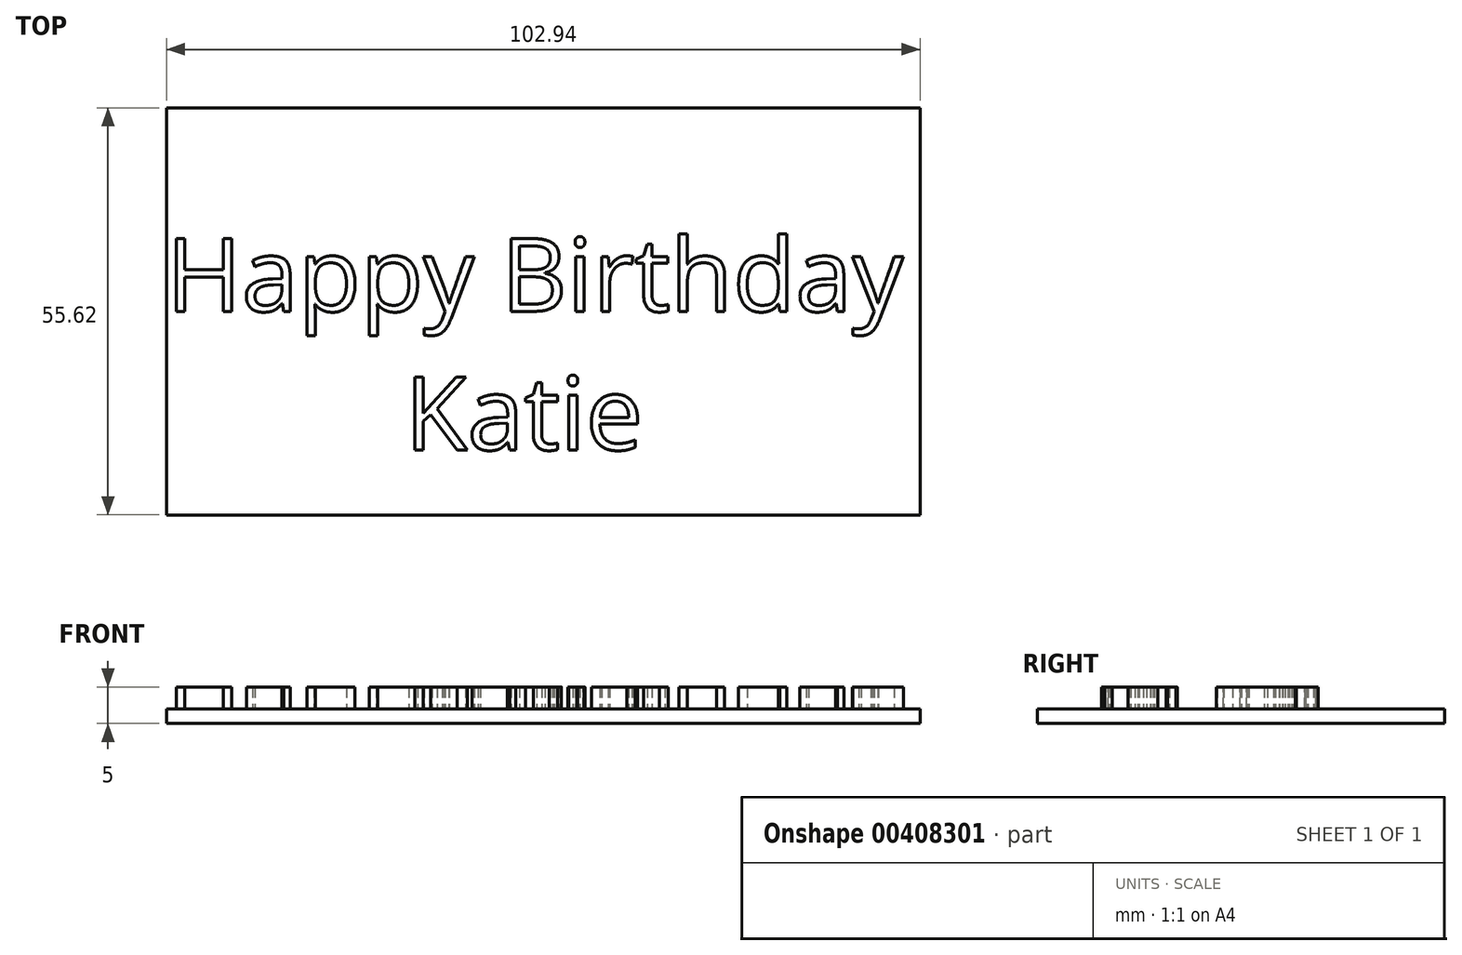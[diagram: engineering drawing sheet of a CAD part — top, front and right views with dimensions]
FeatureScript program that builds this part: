
annotation { "Feature Type Name" : "Feature", "Feature Type Description" : "" }
export const myFeature = defineFeature(function(context is Context, id is Id, definition is map)
    precondition{}
    {
        {
            var Q0;
            Q0=qCreatedBy(makeId("Top.planeOp"),FACE);
            var sketch = newSketch(context, id + "F0", { "sketchPlane" : qUnion([Q0])});
            skLineSegment(sketch, "E0.bottom", {"start": v(-50.3, 25.04) * mm, "end": v(52.64, 25.04) * mm});
            skLineSegment(sketch, "E0.top", {"start": v(-50.3, -30.58) * mm, "end": v(52.64, -30.58) * mm});
            skLineSegment(sketch, "E0.left", {"start": v(-50.3, 25.04) * mm, "end": v(-50.3, -30.58) * mm});
            skLineSegment(sketch, "E0.right", {"start": v(52.64, 25.04) * mm, "end": v(52.64, -30.58) * mm});
            skSolve(sketch);
        }
        {
            var Q0;
            Q0=makeQuery(id+"F0.imprint","IMPRINT",FACE,{"disambiguationData":[TD([[makeQuery(id+"F0.imprint","IMPRINT",EDGE,{"derivedFrom":sQuery(id+"F0.wireOp",EDGE,"E0.bottom")}),-1.0]])]});
            extrude(context, id + "F1", {"entities" : qUnion([Q0]), "depth" : 2 * mm});
        }
        {
            var Q0;
            Q0=makeQuery(id+"F1.opExtrude","CAP_FACE",FACE,{"disambiguationData":[OSD([sQuery(id+"F0.wireOp",EDGE,"E0.bottom"),sQuery(id+"F0.wireOp",EDGE,"E0.top"),sQuery(id+"F0.wireOp",EDGE,"E0.left"),sQuery(id+"F0.wireOp",EDGE,"E0.right")])],"isStart":false});
            var sketch = newSketch(context, id + "F2", { "sketchPlane" : qUnion([Q0])});
            skText(sketch, "E1", { "text": "Happy Birthday\n         Katie", "fontName": "OpenSans-Regular.ttf"});
            skPoint(sketch, "E2", {"position": v(-50.3, -2.77) * mm});
            const initialGuessF2  = {"E1": [-0.0503, -0.00277, 1, 0, 0.01002]};
            skSetInitialGuess(sketch, initialGuessF2);
            skSolve(sketch);
        }
        {
            var Q0;
            Q0 = qSketchRegion(id + "F2", true);
            extrude(context, id + "F3", {"entities" : qUnion([Q0]), "operationType" : NewBodyOperationType.ADD, "depth" : 3 * mm});
        }
    });
